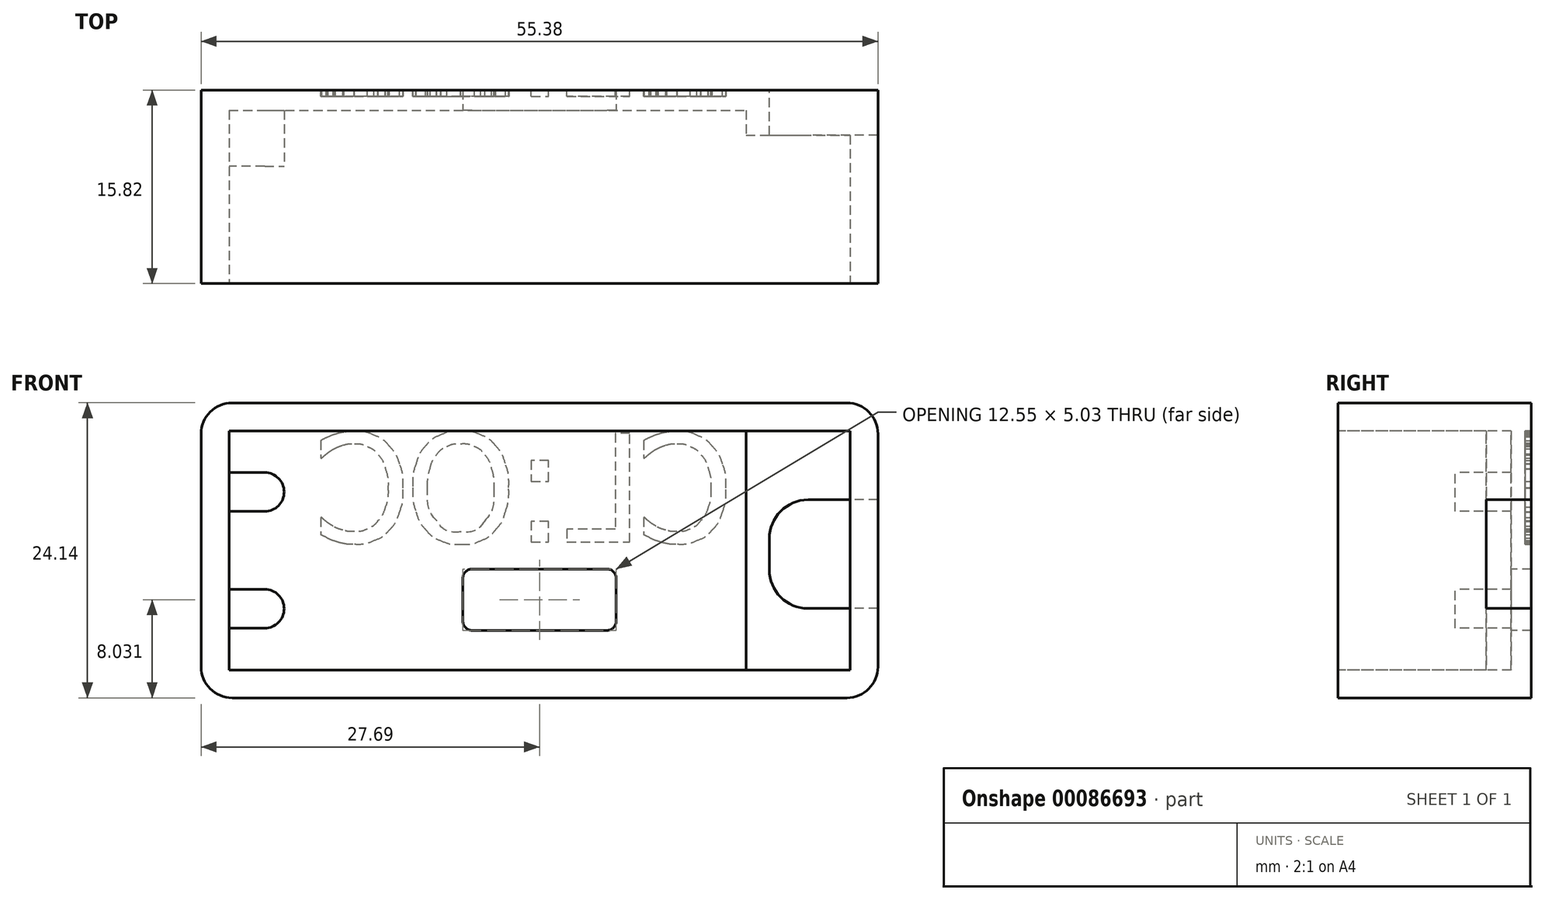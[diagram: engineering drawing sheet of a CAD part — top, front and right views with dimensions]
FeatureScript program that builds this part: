
annotation { "Feature Type Name" : "Feature", "Feature Type Description" : "" }
export const myFeature = defineFeature(function(context is Context, id is Id, definition is map)
    precondition{}
    {
        {
            var Q0;
            Q0=qCreatedBy(makeId("Front.planeOp"),FACE);
            var sketch = newSketch(context, id + "F0", { "sketchPlane" : qUnion([Q0])});
            skLineSegment(sketch, "E0.bottom", {"start": v(-27.69, -12.07) * mm, "end": v(27.69, -12.07) * mm});
            skLineSegment(sketch, "E0.top", {"start": v(-27.69, 12.07) * mm, "end": v(27.69, 12.07) * mm});
            skLineSegment(sketch, "E0.left", {"start": v(-27.69, -12.07) * mm, "end": v(-27.69, 12.07) * mm});
            skLineSegment(sketch, "E0.right", {"start": v(27.69, -12.06) * mm, "end": v(27.69, 12.06) * mm});
            skLineSegment(sketch, "E1.bottom", {"start": v(-26.54, -10.92) * mm, "end": v(26.54, -10.92) * mm});
            skLineSegment(sketch, "E1.top", {"start": v(-26.54, 10.92) * mm, "end": v(26.54, 10.92) * mm});
            skLineSegment(sketch, "E1.left", {"start": v(-26.54, -10.92) * mm, "end": v(-26.54, 10.92) * mm});
            skLineSegment(sketch, "E1.right", {"start": v(26.54, -10.92) * mm, "end": v(26.54, 10.92) * mm});
            skLineSegment(sketch, "E2.bottom", {"start": v(-25.4, -9.78) * mm, "end": v(25.4, -9.78) * mm});
            skLineSegment(sketch, "E2.top", {"start": v(-25.4, 9.78) * mm, "end": v(25.4, 9.78) * mm});
            skLineSegment(sketch, "E2.left", {"start": v(-25.4, -9.78) * mm, "end": v(-25.4, 9.78) * mm});
            skLineSegment(sketch, "E2.right", {"start": v(25.4, -9.78) * mm, "end": v(25.4, 9.78) * mm});
            skLineSegment(sketch, "E3", {"start": v(-36.7, 0) * mm, "end": v(49.4, 0) * mm, "construction": true});
            skLineSegment(sketch, "E4", {"start": v(0, 27.4) * mm, "end": v(0, -29.02) * mm, "construction": true});
            skLineSegment(sketch, "E5", {"start": v(16.9, 9.78) * mm, "end": v(16.9, -9.78) * mm});
            skArc(sketch, "E6", {"start": v(-22.48, 3.19) * mm, "mid": v(-20.9, 4.78) * mm, "end": v(-22.48, 6.36) * mm});
            skCircle(sketch, "E7", {"center": v(22.1, -1.9) * mm, "radius": 3.3 * mm});
            skLineSegment(sketch, "E8.bottom", {"start": v(-6.27, -1.52) * mm, "end": v(6.27, -1.52) * mm});
            skLineSegment(sketch, "E8.top", {"start": v(-6.27, -6.55) * mm, "end": v(6.27, -6.55) * mm});
            skLineSegment(sketch, "E8.left", {"start": v(-6.27, -1.52) * mm, "end": v(-6.27, -6.55) * mm});
            skLineSegment(sketch, "E8.right", {"start": v(6.27, -1.52) * mm, "end": v(6.27, -6.55) * mm});
            skLineSegment(sketch, "E9", {"start": v(-22.48, 6.36) * mm, "end": v(-25.4, 6.36) * mm});
            skLineSegment(sketch, "E10", {"start": v(-22.48, 3.19) * mm, "end": v(-25.4, 3.19) * mm});
            skLineSegment(sketch, "E11.MirrorCS", {"start": v(-22.48, -6.36) * mm, "end": v(-25.4, -6.36) * mm});
            skArc(sketch, "E12.MirrorCS", {"start": v(-22.48, -3.19) * mm, "mid": v(-20.9, -4.78) * mm, "end": v(-22.48, -6.36) * mm});
            skLineSegment(sketch, "E13.MirrorCS", {"start": v(-22.48, -3.19) * mm, "end": v(-25.4, -3.19) * mm});
            skSolve(sketch);
        }
        {
            var Q0;
            {var subQ0=sQuery(id+"F0.wireOp",EDGE,"E7");var subQ1=sQuery(id+"F0.wireOp",EDGE,"E2.right");var subQ2=makeQuery(id+"F0.imprint","INTERSECT",VERTEX,{"disambiguationData":[OD(0.0)],"derivedFrom":[subQ1,subQ0]});Q0=makeQuery(id+"F0.imprint","IMPRINT",FACE,{"disambiguationData":[TD([[makeQuery(id+"F0.imprint","IMPRINT",EDGE,{"disambiguationData":[TD([[subQ2,-1.0]])],"derivedFrom":subQ1}),1.0]])]});}
            var Q1;
            Q1=makeQuery(id+"F0.imprint","IMPRINT",FACE,{"disambiguationData":[TD([[makeQuery(id+"F0.imprint","IMPRINT",EDGE,{"derivedFrom":sQuery(id+"F0.wireOp",EDGE,"E6")}),1.0]])]});
            var Q2;
            Q2=makeQuery(id+"F0.imprint","IMPRINT",FACE,{"disambiguationData":[TD([[makeQuery(id+"F0.imprint","IMPRINT",EDGE,{"derivedFrom":sQuery(id+"F0.wireOp",EDGE,"E8.bottom")}),-1.0]])]});
            var Q3;
            Q3=makeQuery(id+"F0.imprint","IMPRINT",FACE,{"disambiguationData":[TD([[makeQuery(id+"F0.imprint","IMPRINT",EDGE,{"derivedFrom":sQuery(id+"F0.wireOp",EDGE,"E1.bottom")}),1.0]])]});
            var Q4;
            {var subQ0=sQuery(id+"F0.wireOp",EDGE,"E5");Q4=makeQuery(id+"F0.imprint","IMPRINT",FACE,{"disambiguationData":[TD([[makeQuery(id+"F0.imprint","IMPRINT",EDGE,{"derivedFrom":subQ0}),-1.0]])]});}
            var Q5;
            {var subQ8=sQuery(id+"F0.wireOp",EDGE,"E5");Q5=makeQuery(id+"F0.imprint","IMPRINT",FACE,{"disambiguationData":[TD([[makeQuery(id+"F0.imprint","IMPRINT",EDGE,{"derivedFrom":subQ8}),1.0]])]});}
            var Q6;
            Q6=makeQuery(id+"F0.imprint","IMPRINT",FACE,{"disambiguationData":[TD([[makeQuery(id+"F0.imprint","IMPRINT",EDGE,{"derivedFrom":sQuery(id+"F0.wireOp",EDGE,"E0.bottom")}),1.0]])]});
            var Q7;
            {var subQ0=sQuery(id+"F0.wireOp",EDGE,"E11.MirrorCS");Q7=makeQuery(id+"F0.imprint","IMPRINT",FACE,{"disambiguationData":[TD([[makeQuery(id+"F0.imprint","IMPRINT",EDGE,{"derivedFrom":subQ0}),-1.0]])]});}
            var Q8;
            {var subQ0=sQuery(id+"F0.wireOp",EDGE,"E7");var subQ1=sQuery(id+"F0.wireOp",EDGE,"E2.right");var subQ2=makeQuery(id+"F0.imprint","INTERSECT",VERTEX,{"disambiguationData":[OD(0.0)],"derivedFrom":[subQ1,subQ0]});Q8=makeQuery(id+"F0.imprint","IMPRINT",FACE,{"disambiguationData":[TD([[makeQuery(id+"F0.imprint","IMPRINT",EDGE,{"disambiguationData":[TD([[subQ2,-1.0]])],"derivedFrom":subQ1}),-1.0]])]});}
            var Q9;
            Q9=makeQuery(id+"F0.imprint","IMPRINT",FACE,{"disambiguationData":[TD([[makeQuery(id+"F0.imprint","IMPRINT",EDGE,{"derivedFrom":sQuery(id+"F0.wireOp",EDGE,"E7")}),1.0]])]});
            extrude(context, id + "F1", {"entities" : qUnion([Q0, Q1, Q2, Q3, Q4, Q5, Q6, Q7, Q8, Q9]), "oppositeDirection" : true, "offsetDistance" : 25.4 * mm, "depth" : 18.82 * mm});
        }
        {
            var Q0;
            {var subQ0=sQuery(id+"F0.wireOp",EDGE,"E5");Q0=makeQuery(id+"F0.imprint","IMPRINT",FACE,{"disambiguationData":[TD([[makeQuery(id+"F0.imprint","IMPRINT",EDGE,{"derivedFrom":subQ0}),-1.0]])]});}
            var Q1;
            Q1=makeQuery(id+"F0.imprint","IMPRINT",FACE,{"disambiguationData":[TD([[makeQuery(id+"F0.imprint","IMPRINT",EDGE,{"derivedFrom":sQuery(id+"F0.wireOp",EDGE,"E6")}),1.0]])]});
            var Q2;
            {var subQ0=sQuery(id+"F0.wireOp",EDGE,"E11.MirrorCS");Q2=makeQuery(id+"F0.imprint","IMPRINT",FACE,{"disambiguationData":[TD([[makeQuery(id+"F0.imprint","IMPRINT",EDGE,{"derivedFrom":subQ0}),-1.0]])]});}
            var Q3;
            Q3=makeQuery(id+"F0.imprint","IMPRINT",FACE,{"disambiguationData":[TD([[makeQuery(id+"F0.imprint","IMPRINT",EDGE,{"derivedFrom":sQuery(id+"F0.wireOp",EDGE,"E8.bottom")}),-1.0]])]});
            extrude(context, id + "F2", {"entities" : qUnion([Q0, Q1, Q2, Q3]), "operationType" : NewBodyOperationType.REMOVE, "oppositeDirection" : true, "depth" : 17.17 * mm});
        }
        {
            var Q0;
            Q0=makeQuery(id+"F0.imprint","IMPRINT",FACE,{"disambiguationData":[TD([[makeQuery(id+"F0.imprint","IMPRINT",EDGE,{"derivedFrom":sQuery(id+"F0.wireOp",EDGE,"E6")}),1.0]])]});
            var Q1;
            {var subQ0=sQuery(id+"F0.wireOp",EDGE,"E11.MirrorCS");Q1=makeQuery(id+"F0.imprint","IMPRINT",FACE,{"disambiguationData":[TD([[makeQuery(id+"F0.imprint","IMPRINT",EDGE,{"derivedFrom":subQ0}),-1.0]])]});}
            extrude(context, id + "F3", {"entities" : qUnion([Q0, Q1]), "operationType" : NewBodyOperationType.ADD, "endBound" : BoundingType.UP_TO_NEXT, "oppositeDirection" : true, "depth" : 25.4 * mm, "hasSecondDirection" : true, "secondDirectionOppositeDirection" : true, "secondDirectionDepth" : 12.6 * mm});
        }
        {
            var Q0;
            Q0=makeQuery(id+"F0.imprint","IMPRINT",FACE,{"disambiguationData":[TD([[makeQuery(id+"F0.imprint","IMPRINT",EDGE,{"derivedFrom":sQuery(id+"F0.wireOp",EDGE,"E8.bottom")}),-1.0]])]});
            extrude(context, id + "F4", {"entities" : qUnion([Q0]), "operationType" : NewBodyOperationType.REMOVE, "endBound" : BoundingType.THROUGH_ALL, "oppositeDirection" : true, "depth" : 25.4 * mm});
        }
        {
            var Q0;
            {var subQ8=sQuery(id+"F0.wireOp",EDGE,"E5");Q0=makeQuery(id+"F0.imprint","IMPRINT",FACE,{"disambiguationData":[TD([[makeQuery(id+"F0.imprint","IMPRINT",EDGE,{"derivedFrom":subQ8}),1.0]])]});}
            var Q1;
            {var subQ0=sQuery(id+"F0.wireOp",EDGE,"E7");var subQ1=sQuery(id+"F0.wireOp",EDGE,"E2.right");var subQ2=makeQuery(id+"F0.imprint","INTERSECT",VERTEX,{"disambiguationData":[OD(0.0)],"derivedFrom":[subQ1,subQ0]});Q1=makeQuery(id+"F0.imprint","IMPRINT",FACE,{"disambiguationData":[TD([[makeQuery(id+"F0.imprint","IMPRINT",EDGE,{"disambiguationData":[TD([[subQ2,-1.0]])],"derivedFrom":subQ1}),1.0]])]});}
            var Q2;
            Q2=makeQuery(id+"F0.imprint","IMPRINT",FACE,{"disambiguationData":[TD([[makeQuery(id+"F0.imprint","IMPRINT",EDGE,{"derivedFrom":sQuery(id+"F0.wireOp",EDGE,"E7")}),1.0]])]});
            extrude(context, id + "F5", {"entities" : qUnion([Q0, Q1, Q2]), "operationType" : NewBodyOperationType.REMOVE, "oppositeDirection" : true, "depth" : 15.14 * mm});
        }
        {
            var Q0;
            Q0=makeQuery(id+"F0.imprint","IMPRINT",FACE,{"disambiguationData":[TD([[makeQuery(id+"F0.imprint","IMPRINT",EDGE,{"derivedFrom":sQuery(id+"F0.wireOp",EDGE,"E1.bottom")}),1.0]])]});
            var Q1;
            {var subQ0=sQuery(id+"F0.wireOp",EDGE,"E7");var subQ1=sQuery(id+"F0.wireOp",EDGE,"E2.right");var subQ2=makeQuery(id+"F0.imprint","INTERSECT",VERTEX,{"disambiguationData":[OD(0.0)],"derivedFrom":[subQ1,subQ0]});Q1=makeQuery(id+"F0.imprint","IMPRINT",FACE,{"disambiguationData":[TD([[makeQuery(id+"F0.imprint","IMPRINT",EDGE,{"disambiguationData":[TD([[subQ2,-1.0]])],"derivedFrom":subQ1}),-1.0]])]});}
            extrude(context, id + "F6", {"entities" : qUnion([Q0, Q1]), "operationType" : NewBodyOperationType.REMOVE, "oppositeDirection" : true, "depth" : 3 * mm});
        }
        {
            var Q0;
            Q0=makeQuery(id+"F6.boolean.opBoolean","COPY",EDGE,{"derivedFrom":makeQuery(id+"F6.opExtrude","SWEPT_EDGE",EDGE,{"disambiguationData":[OSD([sQuery(id+"F0.wireOp",EDGE,"E1.top"),sQuery(id+"F0.wireOp",EDGE,"E1.left")])]})});
            var Q1;
            Q1=makeQuery(id+"F6.boolean.opBoolean","COPY",EDGE,{"derivedFrom":makeQuery(id+"F6.opExtrude","SWEPT_EDGE",EDGE,{"disambiguationData":[OSD([sQuery(id+"F0.wireOp",EDGE,"E1.top"),sQuery(id+"F0.wireOp",EDGE,"E1.right")])]})});
            var Q2;
            Q2=makeQuery(id+"F6.boolean.opBoolean","COPY",EDGE,{"derivedFrom":makeQuery(id+"F6.opExtrude","SWEPT_EDGE",EDGE,{"disambiguationData":[OSD([sQuery(id+"F0.wireOp",EDGE,"E1.bottom"),sQuery(id+"F0.wireOp",EDGE,"E1.right")])]})});
            var Q3;
            Q3=makeQuery(id+"F6.boolean.opBoolean","COPY",EDGE,{"derivedFrom":makeQuery(id+"F6.opExtrude","SWEPT_EDGE",EDGE,{"disambiguationData":[OSD([sQuery(id+"F0.wireOp",EDGE,"E1.bottom"),sQuery(id+"F0.wireOp",EDGE,"E1.left")])]})});
            fillet(context, id + "F7", {"entities" : qUnion([Q0, Q1, Q2, Q3]), "radius" : 1.4 * mm, "tangentPropagation" : true, "allowEdgeOverflow" : false});
        }
        {
            var Q0;
            Q0=makeQuery(id+"F1.opExtrude","SWEPT_EDGE",EDGE,{"disambiguationData":[OSD([sQuery(id+"F0.wireOp",EDGE,"E0.top"),sQuery(id+"F0.wireOp",EDGE,"E0.right")])]});
            var Q1;
            Q1=makeQuery(id+"F1.opExtrude","SWEPT_EDGE",EDGE,{"disambiguationData":[OSD([sQuery(id+"F0.wireOp",EDGE,"E0.bottom"),sQuery(id+"F0.wireOp",EDGE,"E0.right")])]});
            var Q2;
            Q2=makeQuery(id+"F1.opExtrude","SWEPT_EDGE",EDGE,{"disambiguationData":[OSD([sQuery(id+"F0.wireOp",EDGE,"E0.bottom"),sQuery(id+"F0.wireOp",EDGE,"E0.left")])]});
            var Q3;
            Q3=makeQuery(id+"F1.opExtrude","SWEPT_EDGE",EDGE,{"disambiguationData":[OSD([sQuery(id+"F0.wireOp",EDGE,"E0.top"),sQuery(id+"F0.wireOp",EDGE,"E0.left")])]});
            fillet(context, id + "F8", {"entities" : qUnion([Q0, Q1, Q2, Q3]), "radius" : 2.54 * mm, "tangentPropagation" : true, "allowEdgeOverflow" : false});
        }
        {
            var Q0;
            Q0=makeQuery(id+"F4.boolean.opBoolean","COPY",EDGE,{"derivedFrom":makeQuery(id+"F4.opExtrude","SWEPT_EDGE",EDGE,{"disambiguationData":[OSD([sQuery(id+"F0.wireOp",EDGE,"E8.bottom"),sQuery(id+"F0.wireOp",EDGE,"E8.left")])]})});
            var Q1;
            Q1=makeQuery(id+"F4.boolean.opBoolean","COPY",EDGE,{"derivedFrom":makeQuery(id+"F4.opExtrude","SWEPT_EDGE",EDGE,{"disambiguationData":[OSD([sQuery(id+"F0.wireOp",EDGE,"E8.top"),sQuery(id+"F0.wireOp",EDGE,"E8.left")])]})});
            var Q2;
            Q2=makeQuery(id+"F4.boolean.opBoolean","COPY",EDGE,{"derivedFrom":makeQuery(id+"F4.opExtrude","SWEPT_EDGE",EDGE,{"disambiguationData":[OSD([sQuery(id+"F0.wireOp",EDGE,"E8.top"),sQuery(id+"F0.wireOp",EDGE,"E8.right")])]})});
            var Q3;
            Q3=makeQuery(id+"F4.boolean.opBoolean","COPY",EDGE,{"derivedFrom":makeQuery(id+"F4.opExtrude","SWEPT_EDGE",EDGE,{"disambiguationData":[OSD([sQuery(id+"F0.wireOp",EDGE,"E8.bottom"),sQuery(id+"F0.wireOp",EDGE,"E8.right")])]})});
            fillet(context, id + "F9", {"entities" : qUnion([Q0, Q1, Q2, Q3]), "radius" : 0.76 * mm, "tangentPropagation" : true, "allowEdgeOverflow" : false});
        }
        {
            var Q0;
            Q0=makeQuery(id+"F5.boolean.opBoolean","COPY",FACE,{"derivedFrom":makeQuery(id+"F5.opExtrude","CAP_FACE",FACE,{"disambiguationData":[OSD([sQuery(id+"F0.wireOp",EDGE,"E2.bottom"),sQuery(id+"F0.wireOp",EDGE,"E2.top"),sQuery(id+"F0.wireOp",EDGE,"E2.right"),sQuery(id+"F0.wireOp",EDGE,"E5")])],"isStart":false})});
            var sketch = newSketch(context, id + "F10", { "sketchPlane" : qUnion([Q0])});
            skCircle(sketch, "E14", {"center": v(22.1, -1.9) * mm, "radius": 2.8 * mm});
            skCircle(sketch, "E15.0", {"center": v(22.1, -1.9) * mm, "radius": 3.3 * mm});
            skSolve(sketch);
        }
        {
            var Q0;
            Q0=makeQuery(id+"F10.imprint","IMPRINT",FACE,{"disambiguationData":[TD([[makeQuery(id+"F10.imprint","IMPRINT",EDGE,{"derivedFrom":sQuery(id+"F10.wireOp",EDGE,"E14")}),-1.0]])]});
            extrude(context, id + "F11", {"entities" : qUnion([Q0]), "operationType" : NewBodyOperationType.ADD, "oppositeDirection" : true, "depth" : 1.57 * mm});
        }
        {
            var Q0;
            {var subQ0=sQuery(id+"F0.wireOp",EDGE,"E0.left");var subQ1=sQuery(id+"F0.wireOp",EDGE,"E0.top");var subQ4=sQuery(id+"F0.wireOp",EDGE,"E0.bottom");var subQ7=sQuery(id+"F0.wireOp",EDGE,"E0.right");Q0=makeQuery(id+"FXK7WlyEqimvF51_1.boolean.opBoolean","SPLIT",FACE,{"disambiguationData":[TD([makeQuery(id+"F1.opExtrude","SWEPT_FACE",FACE,{"disambiguationData":[OSD([subQ4])]})])],"derivedFrom":makeQuery(id+"F1.opExtrude","CAP_FACE",FACE,{"disambiguationData":[OSD([subQ4,subQ1,subQ0,subQ7])],"isStart":false})});}
            var sketch = newSketch(context, id + "F12", { "sketchPlane" : qUnion([Q0])});
            skFitSpline(sketch, "E16", {"points": [v(-11.27, 0.51) * mm, v(-11.85, 0.51) * mm, v(-12.39, 0.61) * mm, v(-12.88, 0.8) * mm]});
            skFitSpline(sketch, "E17", {"points": [v(-12.88, 0.8) * mm, v(-13.36, 1) * mm, v(-13.78, 1.3) * mm, v(-14.14, 1.68) * mm]});
            skFitSpline(sketch, "E18", {"points": [v(-14.14, 1.68) * mm, v(-14.49, 2.06) * mm, v(-14.76, 2.55) * mm, v(-14.96, 3.12) * mm]});
            skFitSpline(sketch, "E19", {"points": [v(-14.96, 3.12) * mm, v(-15.15, 3.7) * mm, v(-15.25, 4.36) * mm, v(-15.25, 5.11) * mm]});
            skFitSpline(sketch, "E20", {"points": [v(-15.25, 5.11) * mm, v(-15.25, 5.86) * mm, v(-15.16, 6.5) * mm, v(-14.97, 7.06) * mm]});
            skFitSpline(sketch, "E21", {"points": [v(-14.97, 7.06) * mm, v(-14.78, 7.61) * mm, v(-14.5, 8.1) * mm, v(-14.14, 8.5) * mm]});
            skFitSpline(sketch, "E22", {"points": [v(-14.14, 8.5) * mm, v(-13.79, 8.9) * mm, v(-13.37, 9.2) * mm, v(-12.88, 9.41) * mm]});
            skFitSpline(sketch, "E23", {"points": [v(-12.88, 9.41) * mm, v(-12.4, 9.62) * mm, v(-11.85, 9.73) * mm, v(-11.25, 9.73) * mm]});
            skFitSpline(sketch, "E24", {"points": [v(-11.25, 9.73) * mm, v(-10.95, 9.73) * mm, v(-10.67, 9.7) * mm, v(-10.42, 9.66) * mm]});
            skFitSpline(sketch, "E25", {"points": [v(-10.42, 9.66) * mm, v(-10.15, 9.62) * mm, v(-9.91, 9.56) * mm, v(-9.69, 9.5) * mm]});
            skFitSpline(sketch, "E26", {"points": [v(-9.69, 9.5) * mm, v(-9.5, 9.43) * mm, v(-9.3, 9.36) * mm, v(-9.1, 9.27) * mm]});
            skFitSpline(sketch, "E27", {"points": [v(-9.1, 9.27) * mm, v(-8.9, 9.18) * mm, v(-8.7, 9.08) * mm, v(-8.5, 8.97) * mm]});
            skFitSpline(sketch, "E28", {"points": [v(-8.6, 7.55) * mm, v(-8.7, 7.64) * mm, v(-8.84, 7.76) * mm, v(-9, 7.9) * mm]});
            skFitSpline(sketch, "E29", {"points": [v(-9, 7.9) * mm, v(-9.16, 8.03) * mm, v(-9.36, 8.16) * mm, v(-9.6, 8.3) * mm]});
            skFitSpline(sketch, "E30", {"points": [v(-9.6, 8.3) * mm, v(-9.82, 8.42) * mm, v(-10.07, 8.52) * mm, v(-10.34, 8.6) * mm]});
            skFitSpline(sketch, "E31", {"points": [v(-10.34, 8.6) * mm, v(-10.6, 8.68) * mm, v(-10.91, 8.72) * mm, v(-11.26, 8.72) * mm]});
            skFitSpline(sketch, "E32", {"points": [v(-11.26, 8.72) * mm, v(-11.64, 8.72) * mm, v(-12, 8.64) * mm, v(-12.34, 8.49) * mm]});
            skFitSpline(sketch, "E33", {"points": [v(-12.34, 8.49) * mm, v(-12.68, 8.33) * mm, v(-12.97, 8.1) * mm, v(-13.23, 7.8) * mm]});
            skFitSpline(sketch, "E34", {"points": [v(-13.23, 7.8) * mm, v(-13.48, 7.5) * mm, v(-13.67, 7.12) * mm, v(-13.81, 6.66) * mm]});
            skFitSpline(sketch, "E35", {"points": [v(-13.81, 6.66) * mm, v(-13.95, 6.2) * mm, v(-14.02, 5.68) * mm, v(-14.02, 5.11) * mm]});
            skFitSpline(sketch, "E36", {"points": [v(-14.02, 5.11) * mm, v(-14.02, 4.5) * mm, v(-13.95, 3.98) * mm, v(-13.8, 3.54) * mm]});
            skFitSpline(sketch, "E37", {"points": [v(-13.8, 3.54) * mm, v(-13.65, 3.1) * mm, v(-13.45, 2.73) * mm, v(-13.2, 2.43) * mm]});
            skFitSpline(sketch, "E38", {"points": [v(-13.2, 2.43) * mm, v(-12.95, 2.13) * mm, v(-12.66, 1.9) * mm, v(-12.33, 1.76) * mm]});
            skFitSpline(sketch, "E39", {"points": [v(-12.33, 1.76) * mm, v(-12, 1.6) * mm, v(-11.64, 1.54) * mm, v(-11.26, 1.54) * mm]});
            skFitSpline(sketch, "E40", {"points": [v(-11.26, 1.54) * mm, v(-10.92, 1.54) * mm, v(-10.6, 1.58) * mm, v(-10.31, 1.66) * mm]});
            skFitSpline(sketch, "E41", {"points": [v(-10.31, 1.66) * mm, v(-10.02, 1.74) * mm, v(-9.76, 1.85) * mm, v(-9.54, 1.98) * mm]});
            skFitSpline(sketch, "E42", {"points": [v(-9.54, 1.98) * mm, v(-9.32, 2.1) * mm, v(-9.13, 2.23) * mm, v(-8.97, 2.35) * mm]});
            skFitSpline(sketch, "E43", {"points": [v(-8.97, 2.35) * mm, v(-8.81, 2.48) * mm, v(-8.69, 2.6) * mm, v(-8.6, 2.69) * mm]});
            skLineSegment(sketch, "E44", {"start": v(-8.5, 8.97) * mm, "end": v(-8.5, 7.55) * mm});
            skLineSegment(sketch, "E45", {"start": v(-8.5, 7.55) * mm, "end": v(-8.6, 7.55) * mm});
            skFitSpline(sketch, "E46", {"points": [v(-8.5, 1.28) * mm, v(-8.7, 1.19) * mm, v(-8.89, 1.1) * mm, v(-9.06, 1.02) * mm]});
            skFitSpline(sketch, "E47", {"points": [v(-9.06, 1.02) * mm, v(-9.23, 0.93) * mm, v(-9.44, 0.85) * mm, v(-9.69, 0.77) * mm]});
            skFitSpline(sketch, "E48", {"points": [v(-9.69, 0.77) * mm, v(-9.95, 0.69) * mm, v(-10.19, 0.62) * mm, v(-10.4, 0.58) * mm]});
            skFitSpline(sketch, "E49", {"points": [v(-10.4, 0.58) * mm, v(-10.63, 0.54) * mm, v(-10.92, 0.51) * mm, v(-11.27, 0.51) * mm]});
            skLineSegment(sketch, "E50", {"start": v(-8.6, 2.69) * mm, "end": v(-8.5, 2.69) * mm});
            skLineSegment(sketch, "E51", {"start": v(-8.5, 2.69) * mm, "end": v(-8.5, 1.28) * mm});
            skLineSegment(sketch, "E52", {"start": v(-2.24, 0.68) * mm, "end": v(-7.39, 0.68) * mm});
            skLineSegment(sketch, "E53", {"start": v(-7.39, 0.68) * mm, "end": v(-7.39, 9.57) * mm});
            skLineSegment(sketch, "E54", {"start": v(-7.39, 9.57) * mm, "end": v(-6.2, 9.57) * mm});
            skLineSegment(sketch, "E55", {"start": v(-6.2, 9.57) * mm, "end": v(-6.2, 1.73) * mm});
            skLineSegment(sketch, "E56", {"start": v(-6.2, 1.73) * mm, "end": v(-2.24, 1.73) * mm});
            skLineSegment(sketch, "E57", {"start": v(-2.24, 1.73) * mm, "end": v(-2.24, 0.68) * mm});
            skLineSegment(sketch, "E58", {"start": v(0.68, 5.64) * mm, "end": v(-0.75, 5.64) * mm});
            skLineSegment(sketch, "E59", {"start": v(-0.75, 5.64) * mm, "end": v(-0.75, 7.34) * mm});
            skLineSegment(sketch, "E60", {"start": v(-0.75, 7.34) * mm, "end": v(0.68, 7.34) * mm});
            skLineSegment(sketch, "E61", {"start": v(0.68, 7.34) * mm, "end": v(0.68, 5.64) * mm});
            skFitSpline(sketch, "E62", {"points": [v(9.31, 8.54) * mm, v(9.65, 8.15) * mm, v(9.91, 7.67) * mm, v(10.1, 7.1) * mm]});
            skFitSpline(sketch, "E63", {"points": [v(10.1, 7.1) * mm, v(10.29, 6.52) * mm, v(10.38, 5.86) * mm, v(10.38, 5.12) * mm]});
            skFitSpline(sketch, "E64", {"points": [v(10.38, 5.12) * mm, v(10.38, 4.4) * mm, v(10.29, 3.75) * mm, v(10.1, 3.17) * mm]});
            skFitSpline(sketch, "E65", {"points": [v(10.1, 3.17) * mm, v(9.92, 2.58) * mm, v(9.66, 2.1) * mm, v(9.31, 1.7) * mm]});
            skFitSpline(sketch, "E66", {"points": [v(9.31, 1.7) * mm, v(8.95, 1.29) * mm, v(8.52, 0.98) * mm, v(8.04, 0.78) * mm]});
            skFitSpline(sketch, "E67", {"points": [v(8.04, 0.78) * mm, v(7.56, 0.59) * mm, v(7.03, 0.5) * mm, v(6.44, 0.5) * mm]});
            skFitSpline(sketch, "E68", {"points": [v(6.44, 0.5) * mm, v(5.84, 0.5) * mm, v(5.3, 0.6) * mm, v(4.82, 0.8) * mm]});
            skFitSpline(sketch, "E69", {"points": [v(4.82, 0.8) * mm, v(4.34, 1) * mm, v(3.93, 1.3) * mm, v(3.58, 1.7) * mm]});
            skFitSpline(sketch, "E70", {"points": [v(3.58, 1.7) * mm, v(3.24, 2.1) * mm, v(2.97, 2.58) * mm, v(2.8, 3.16) * mm]});
            skFitSpline(sketch, "E71", {"points": [v(2.8, 3.16) * mm, v(2.6, 3.74) * mm, v(2.52, 4.39) * mm, v(2.52, 5.12) * mm]});
            skFitSpline(sketch, "E72", {"points": [v(2.52, 5.12) * mm, v(2.52, 5.87) * mm, v(2.6, 6.52) * mm, v(2.8, 7.09) * mm]});
            skFitSpline(sketch, "E73", {"points": [v(2.8, 7.09) * mm, v(2.98, 7.65) * mm, v(3.24, 8.14) * mm, v(3.59, 8.54) * mm]});
            skFitSpline(sketch, "E74", {"points": [v(3.59, 8.54) * mm, v(3.93, 8.94) * mm, v(4.34, 9.24) * mm, v(4.82, 9.44) * mm]});
            skFitSpline(sketch, "E75", {"points": [v(4.82, 9.44) * mm, v(5.3, 9.65) * mm, v(5.85, 9.75) * mm, v(6.44, 9.75) * mm]});
            skFitSpline(sketch, "E76", {"points": [v(6.44, 9.75) * mm, v(7.05, 9.75) * mm, v(7.6, 9.65) * mm, v(8.08, 9.43) * mm]});
            skFitSpline(sketch, "E77", {"points": [v(8.08, 9.43) * mm, v(8.57, 9.22) * mm, v(8.98, 8.93) * mm, v(9.31, 8.54) * mm]});
            skLineSegment(sketch, "E78", {"start": v(0.68, 0.68) * mm, "end": v(-0.75, 0.68) * mm});
            skLineSegment(sketch, "E79", {"start": v(-0.75, 0.68) * mm, "end": v(-0.75, 2.38) * mm});
            skLineSegment(sketch, "E80", {"start": v(-0.75, 2.38) * mm, "end": v(0.68, 2.38) * mm});
            skLineSegment(sketch, "E81", {"start": v(0.68, 2.38) * mm, "end": v(0.68, 0.68) * mm});
            skFitSpline(sketch, "E82", {"points": [v(9.15, 5.12) * mm, v(9.15, 5.7) * mm, v(9.09, 6.23) * mm, v(8.96, 6.68) * mm]});
            skFitSpline(sketch, "E83", {"points": [v(8.96, 6.68) * mm, v(8.83, 7.14) * mm, v(8.65, 7.51) * mm, v(8.42, 7.81) * mm]});
            skFitSpline(sketch, "E84", {"points": [v(8.42, 7.81) * mm, v(8.19, 8.12) * mm, v(7.9, 8.35) * mm, v(7.57, 8.5) * mm]});
            skFitSpline(sketch, "E85", {"points": [v(7.57, 8.5) * mm, v(7.24, 8.65) * mm, v(6.86, 8.73) * mm, v(6.45, 8.73) * mm]});
            skFitSpline(sketch, "E86", {"points": [v(6.45, 8.73) * mm, v(6.02, 8.73) * mm, v(5.64, 8.65) * mm, v(5.32, 8.5) * mm]});
            skFitSpline(sketch, "E87", {"points": [v(5.32, 8.5) * mm, v(5, 8.36) * mm, v(4.72, 8.12) * mm, v(4.47, 7.81) * mm]});
            skFitSpline(sketch, "E88", {"points": [v(4.47, 7.81) * mm, v(4.24, 7.5) * mm, v(4.06, 7.13) * mm, v(3.93, 6.67) * mm]});
            skFitSpline(sketch, "E89", {"points": [v(3.93, 6.67) * mm, v(3.8, 6.21) * mm, v(3.75, 5.7) * mm, v(3.75, 5.12) * mm]});
            skFitSpline(sketch, "E90", {"points": [v(3.75, 5.12) * mm, v(3.75, 3.95) * mm, v(4, 3.06) * mm, v(4.48, 2.44) * mm]});
            skFitSpline(sketch, "E91", {"points": [v(4.48, 2.44) * mm, v(4.97, 1.82) * mm, v(5.63, 1.51) * mm, v(6.45, 1.51) * mm]});
            skFitSpline(sketch, "E92", {"points": [v(6.45, 1.51) * mm, v(7.27, 1.51) * mm, v(7.93, 1.82) * mm, v(8.42, 2.44) * mm]});
            skFitSpline(sketch, "E93", {"points": [v(8.42, 2.44) * mm, v(8.9, 3.06) * mm, v(9.15, 3.95) * mm, v(9.15, 5.12) * mm]});
            skFitSpline(sketch, "E94", {"points": [v(15.14, 0.51) * mm, v(14.56, 0.51) * mm, v(14.03, 0.61) * mm, v(13.54, 0.8) * mm]});
            skFitSpline(sketch, "E95", {"points": [v(13.54, 0.8) * mm, v(13.05, 1) * mm, v(12.63, 1.3) * mm, v(12.28, 1.68) * mm]});
            skFitSpline(sketch, "E96", {"points": [v(12.28, 1.68) * mm, v(11.92, 2.06) * mm, v(11.65, 2.55) * mm, v(11.45, 3.12) * mm]});
            skFitSpline(sketch, "E97", {"points": [v(11.45, 3.12) * mm, v(11.26, 3.7) * mm, v(11.16, 4.36) * mm, v(11.16, 5.11) * mm]});
            skFitSpline(sketch, "E98", {"points": [v(11.16, 5.11) * mm, v(11.16, 5.86) * mm, v(11.26, 6.5) * mm, v(11.44, 7.06) * mm]});
            skFitSpline(sketch, "E99", {"points": [v(11.44, 7.06) * mm, v(11.63, 7.61) * mm, v(11.9, 8.1) * mm, v(12.27, 8.5) * mm]});
            skFitSpline(sketch, "E100", {"points": [v(12.27, 8.5) * mm, v(12.63, 8.9) * mm, v(13.05, 9.2) * mm, v(13.53, 9.41) * mm]});
            skFitSpline(sketch, "E101", {"points": [v(13.53, 9.41) * mm, v(14.02, 9.62) * mm, v(14.56, 9.73) * mm, v(15.16, 9.73) * mm]});
            skFitSpline(sketch, "E102", {"points": [v(15.16, 9.73) * mm, v(15.46, 9.73) * mm, v(15.74, 9.7) * mm, v(16, 9.66) * mm]});
            skFitSpline(sketch, "E103", {"points": [v(16, 9.66) * mm, v(16.26, 9.62) * mm, v(16.5, 9.56) * mm, v(16.73, 9.5) * mm]});
            skFitSpline(sketch, "E104", {"points": [v(16.73, 9.5) * mm, v(16.92, 9.43) * mm, v(17.11, 9.36) * mm, v(17.31, 9.27) * mm]});
            skFitSpline(sketch, "E105", {"points": [v(17.31, 9.27) * mm, v(17.51, 9.18) * mm, v(17.71, 9.08) * mm, v(17.9, 8.97) * mm]});
            skFitSpline(sketch, "E106", {"points": [v(17.81, 7.55) * mm, v(17.7, 7.64) * mm, v(17.58, 7.76) * mm, v(17.41, 7.9) * mm]});
            skFitSpline(sketch, "E107", {"points": [v(17.41, 7.9) * mm, v(17.25, 8.03) * mm, v(17.05, 8.16) * mm, v(16.82, 8.3) * mm]});
            skFitSpline(sketch, "E108", {"points": [v(16.82, 8.3) * mm, v(16.59, 8.42) * mm, v(16.34, 8.52) * mm, v(16.08, 8.6) * mm]});
            skFitSpline(sketch, "E109", {"points": [v(16.08, 8.6) * mm, v(15.8, 8.68) * mm, v(15.5, 8.72) * mm, v(15.15, 8.72) * mm]});
            skFitSpline(sketch, "E110", {"points": [v(15.15, 8.72) * mm, v(14.77, 8.72) * mm, v(14.41, 8.64) * mm, v(14.08, 8.49) * mm]});
            skFitSpline(sketch, "E111", {"points": [v(14.08, 8.49) * mm, v(13.74, 8.33) * mm, v(13.44, 8.1) * mm, v(13.19, 7.8) * mm]});
            skFitSpline(sketch, "E112", {"points": [v(13.19, 7.8) * mm, v(12.93, 7.5) * mm, v(12.74, 7.12) * mm, v(12.6, 6.66) * mm]});
            skFitSpline(sketch, "E113", {"points": [v(12.6, 6.66) * mm, v(12.46, 6.2) * mm, v(12.4, 5.68) * mm, v(12.4, 5.11) * mm]});
            skFitSpline(sketch, "E114", {"points": [v(12.4, 5.11) * mm, v(12.4, 4.5) * mm, v(12.47, 3.98) * mm, v(12.61, 3.54) * mm]});
            skFitSpline(sketch, "E115", {"points": [v(12.61, 3.54) * mm, v(12.76, 3.1) * mm, v(12.96, 2.73) * mm, v(13.22, 2.43) * mm]});
            skFitSpline(sketch, "E116", {"points": [v(13.22, 2.43) * mm, v(13.46, 2.13) * mm, v(13.75, 1.9) * mm, v(14.09, 1.76) * mm]});
            skFitSpline(sketch, "E117", {"points": [v(14.09, 1.76) * mm, v(14.42, 1.6) * mm, v(14.78, 1.54) * mm, v(15.15, 1.54) * mm]});
            skFitSpline(sketch, "E118", {"points": [v(15.15, 1.54) * mm, v(15.5, 1.54) * mm, v(15.8, 1.58) * mm, v(16.1, 1.66) * mm]});
            skFitSpline(sketch, "E119", {"points": [v(16.1, 1.66) * mm, v(16.39, 1.74) * mm, v(16.65, 1.85) * mm, v(16.88, 1.98) * mm]});
            skFitSpline(sketch, "E120", {"points": [v(16.88, 1.98) * mm, v(17.1, 2.1) * mm, v(17.28, 2.23) * mm, v(17.44, 2.35) * mm]});
            skFitSpline(sketch, "E121", {"points": [v(17.44, 2.35) * mm, v(17.6, 2.48) * mm, v(17.73, 2.6) * mm, v(17.82, 2.69) * mm]});
            skLineSegment(sketch, "E122", {"start": v(17.9, 8.97) * mm, "end": v(17.9, 7.55) * mm});
            skLineSegment(sketch, "E123", {"start": v(17.9, 7.55) * mm, "end": v(17.81, 7.55) * mm});
            skFitSpline(sketch, "E124", {"points": [v(17.9, 1.28) * mm, v(17.71, 1.19) * mm, v(17.53, 1.1) * mm, v(17.35, 1.02) * mm]});
            skFitSpline(sketch, "E125", {"points": [v(17.35, 1.02) * mm, v(17.18, 0.93) * mm, v(16.97, 0.85) * mm, v(16.73, 0.77) * mm]});
            skFitSpline(sketch, "E126", {"points": [v(16.73, 0.77) * mm, v(16.47, 0.69) * mm, v(16.23, 0.62) * mm, v(16, 0.58) * mm]});
            skFitSpline(sketch, "E127", {"points": [v(16, 0.58) * mm, v(15.78, 0.54) * mm, v(15.5, 0.51) * mm, v(15.14, 0.51) * mm]});
            skLineSegment(sketch, "E128", {"start": v(17.82, 2.69) * mm, "end": v(17.9, 2.69) * mm});
            skLineSegment(sketch, "E129", {"start": v(17.9, 2.69) * mm, "end": v(17.9, 1.28) * mm});
            skSolve(sketch);
        }
        {
            var Q0;
            Q0 = qSketchRegion(id + "F12", true);
            extrude(context, id + "F13", {"entities" : qUnion([Q0]), "operationType" : NewBodyOperationType.REMOVE, "oppositeDirection" : true, "depth" : 0.5 * mm});
        }
        {
            var Q0;
            {var subQ2=sQuery(id+"F0.wireOp",EDGE,"E0.left");var subQ3=sQuery(id+"F0.wireOp",EDGE,"E0.bottom");var subQ4=sQuery(id+"F0.wireOp",EDGE,"E0.top");var subQ5=sQuery(id+"F0.wireOp",EDGE,"E0.right");Q0=makeQuery(id+"F13.boolean.opBoolean","SPLIT",FACE,{"disambiguationData":[TD([makeQuery(id+"F1.opExtrude","SWEPT_FACE",FACE,{"disambiguationData":[OSD([subQ3])]})])],"derivedFrom":makeQuery(id+"F1.opExtrude","CAP_FACE",FACE,{"disambiguationData":[OSD([subQ3,subQ4,subQ2,subQ5])],"isStart":false})});}
            var sketch = newSketch(context, id + "F14", { "sketchPlane" : qUnion([Q0])});
            skLineSegment(sketch, "E130.bottom", {"start": v(-27.69, 4.13) * mm, "end": v(-21.97, 4.13) * mm});
            skLineSegment(sketch, "E130.top", {"start": v(-27.69, -4.76) * mm, "end": v(-21.97, -4.76) * mm});
            skLineSegment(sketch, "E130.left", {"start": v(-27.69, 4.13) * mm, "end": v(-27.69, -4.76) * mm});
            skLineSegment(sketch, "E130.right", {"start": v(-18.8, 0.96) * mm, "end": v(-18.8, -1.58) * mm});
            skPoint(sketch, "E131.visualSharp", {"position": v(-18.8, 4.13) * mm});
            skArc(sketch, "E131.filletArc", {"start": v(-18.8, 0.96) * mm, "mid": v(-19.73, 3.2) * mm, "end": v(-21.97, 4.13) * mm});
            skPoint(sketch, "E132.visualSharp", {"position": v(-18.8, -4.76) * mm});
            skArc(sketch, "E132.filletArc", {"start": v(-21.97, -4.76) * mm, "mid": v(-19.73, -3.83) * mm, "end": v(-18.8, -1.58) * mm});
            skSolve(sketch);
        }
        {
            var Q0;
            Q0 = qSketchRegion(id + "F14", true);
            var Q1;
            Q1=makeQuery(id+"F5.boolean.opBoolean","COPY",FACE,{"derivedFrom":makeQuery(id+"F5.opExtrude","CAP_FACE",FACE,{"disambiguationData":[OSD([sQuery(id+"F0.wireOp",EDGE,"E2.bottom"),sQuery(id+"F0.wireOp",EDGE,"E2.top"),sQuery(id+"F0.wireOp",EDGE,"E2.right"),sQuery(id+"F0.wireOp",EDGE,"E5")])],"isStart":false})});
            extrude(context, id + "F15", {"entities" : qUnion([Q0]), "operationType" : NewBodyOperationType.REMOVE, "endBound" : BoundingType.UP_TO_SURFACE, "oppositeDirection" : true, "depth" : 25.4 * mm, "endBoundEntityFace" : qUnion([Q1]), "offsetDistance" : 25.4 * mm});
        }
        {
            var Q0;
            Q0=makeQuery(id+"F1.opExtrude","CAP_FACE",FACE,{"disambiguationData":[OSD([sQuery(id+"F0.wireOp",EDGE,"E0.bottom"),sQuery(id+"F0.wireOp",EDGE,"E0.top"),sQuery(id+"F0.wireOp",EDGE,"E0.left"),sQuery(id+"F0.wireOp",EDGE,"E0.right")])],"isStart":true});
            var sketch = newSketch(context, id + "F16", { "sketchPlane" : qUnion([Q0])});
            skLineSegment(sketch, "E133.0.0", {"start": v(25.15, 12.07) * mm, "end": v(-25.15, 12.07) * mm});
            skArc(sketch, "E133.0.1", {"start": v(-25.15, 12.07) * mm, "mid": v(-26.94, 11.32) * mm, "end": v(-27.69, 9.53) * mm});
            skLineSegment(sketch, "E133.0.2", {"start": v(-27.69, 9.53) * mm, "end": v(-27.69, -9.53) * mm});
            skArc(sketch, "E133.0.3", {"start": v(-27.69, -9.53) * mm, "mid": v(-26.94, -11.32) * mm, "end": v(-25.15, -12.07) * mm});
            skLineSegment(sketch, "E133.0.4", {"start": v(-25.15, -12.07) * mm, "end": v(25.15, -12.07) * mm});
            skArc(sketch, "E133.0.5", {"start": v(25.15, -12.07) * mm, "mid": v(26.94, -11.32) * mm, "end": v(27.69, -9.53) * mm});
            skLineSegment(sketch, "E133.0.6", {"start": v(27.69, -9.53) * mm, "end": v(27.69, 9.53) * mm});
            skArc(sketch, "E133.0.7", {"start": v(27.69, 9.53) * mm, "mid": v(26.94, 11.32) * mm, "end": v(25.15, 12.07) * mm});
            skSolve(sketch);
        }
        {
            var Q0;
            Q0 = qSketchRegion(id + "F16", true);
            var Q1;
            Q1=makeQuery(id+"F6.boolean.opBoolean","COPY",FACE,{"derivedFrom":makeQuery(id+"F6.opExtrude","CAP_FACE",FACE,{"disambiguationData":[OSD([sQuery(id+"F0.wireOp",EDGE,"E1.bottom"),sQuery(id+"F0.wireOp",EDGE,"E1.top"),sQuery(id+"F0.wireOp",EDGE,"E1.left"),sQuery(id+"F0.wireOp",EDGE,"E1.right"),sQuery(id+"F0.wireOp",EDGE,"E2.bottom"),sQuery(id+"F0.wireOp",EDGE,"E2.top"),sQuery(id+"F0.wireOp",EDGE,"E2.left"),sQuery(id+"F0.wireOp",EDGE,"E2.right")])],"isStart":false})});
            extrude(context, id + "F17", {"entities" : qUnion([Q0]), "operationType" : NewBodyOperationType.REMOVE, "endBound" : BoundingType.UP_TO_SURFACE, "oppositeDirection" : true, "depth" : 25.4 * mm, "endBoundEntityFace" : qUnion([Q1]), "offsetDistance" : 25.4 * mm});
        }
    });
